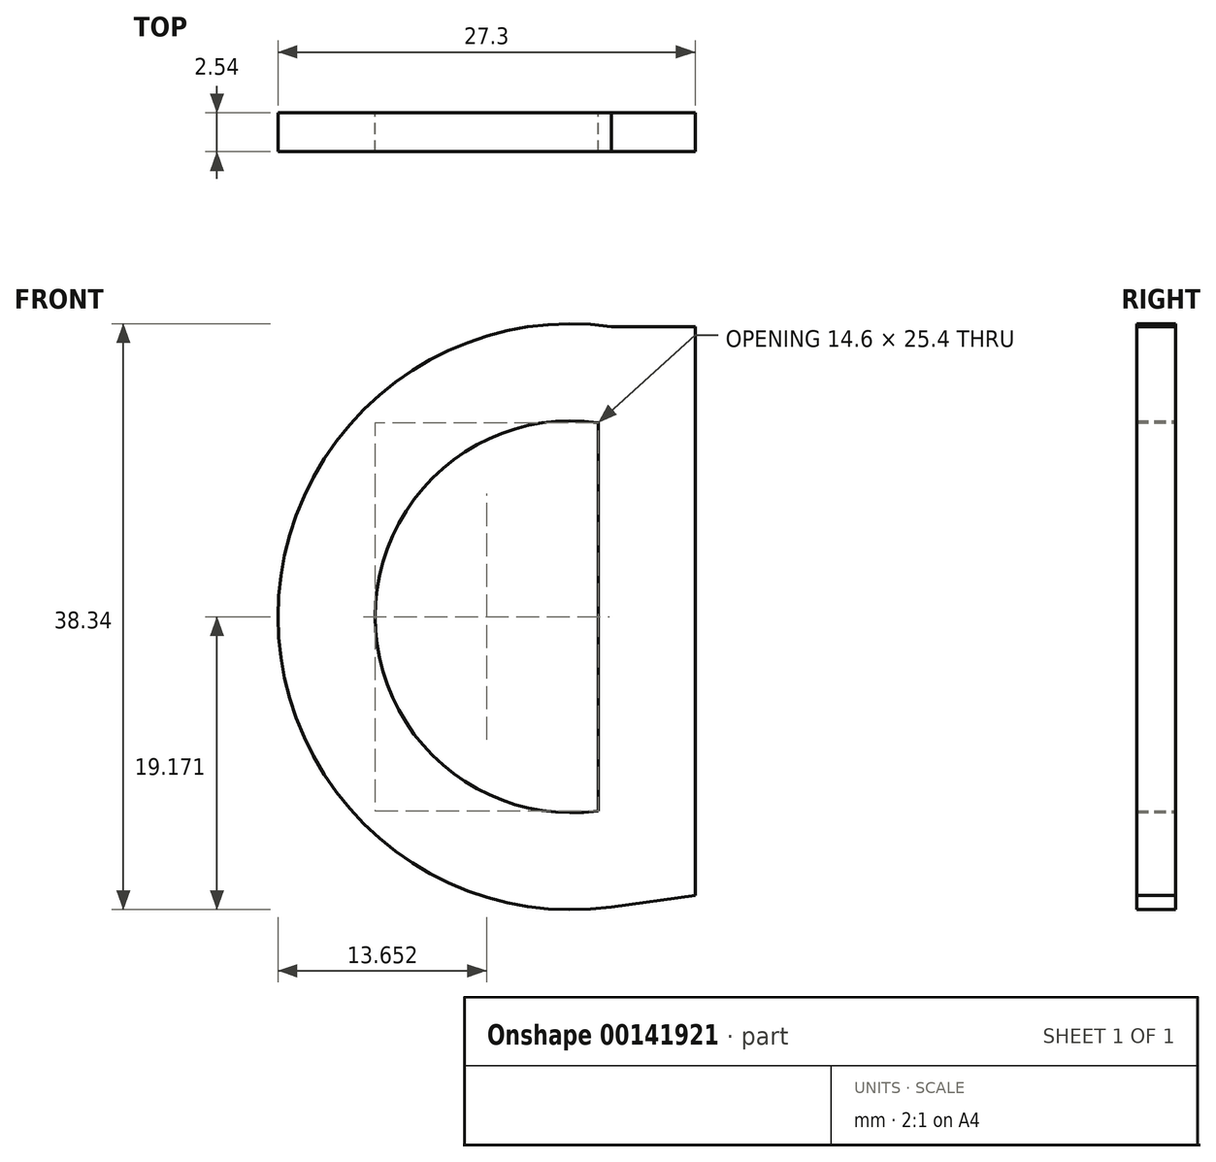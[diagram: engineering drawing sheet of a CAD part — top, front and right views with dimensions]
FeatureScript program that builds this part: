
annotation { "Feature Type Name" : "Feature", "Feature Type Description" : "" }
export const myFeature = defineFeature(function(context is Context, id is Id, definition is map)
    precondition{}
    {
        {
            var Q0;
            Q0=qCreatedBy(makeId("Front.planeOp"),FACE);
            var sketch = newSketch(context, id + "F0", { "sketchPlane" : qUnion([Q0])});
            skLineSegment(sketch, "E0", {"start": v(0, 14) * mm, "end": v(0, -11.4) * mm});
            skArc(sketch, "E1", {"start": v(0, 14) * mm, "mid": v(-14.6, 1.3) * mm, "end": v(0, -11.4) * mm});
            skArc(sketch, "E2.0", {"start": v(0.88, 20.29) * mm, "mid": v(-20.95, 1.3) * mm, "end": v(0.88, -17.69) * mm});
            skLineSegment(sketch, "E3.0", {"start": v(6.35, 14) * mm, "end": v(6.35, -11.4) * mm});
            skLineSegment(sketch, "E4", {"start": v(0.88, 20.29) * mm, "end": v(6.35, 20.29) * mm});
            skLineSegment(sketch, "E5", {"start": v(6.35, 20.29) * mm, "end": v(6.35, 14) * mm});
            skLineSegment(sketch, "E6", {"start": v(0.88, -17.69) * mm, "end": v(6.35, -16.92) * mm});
            skLineSegment(sketch, "E7", {"start": v(6.35, -16.92) * mm, "end": v(6.35, -11.4) * mm});
            skSolve(sketch);
        }
        {
            var Q0;
            Q0=makeQuery(id+"F0.imprint","IMPRINT",FACE,{"disambiguationData":[TD([[makeQuery(id+"F0.imprint","IMPRINT",EDGE,{"derivedFrom":sQuery(id+"F0.wireOp",EDGE,"E0")}),1.0]])]});
            extrude(context, id + "F1", {"entities" : qUnion([Q0]), "depth" : 2.54 * mm});
        }
    });
